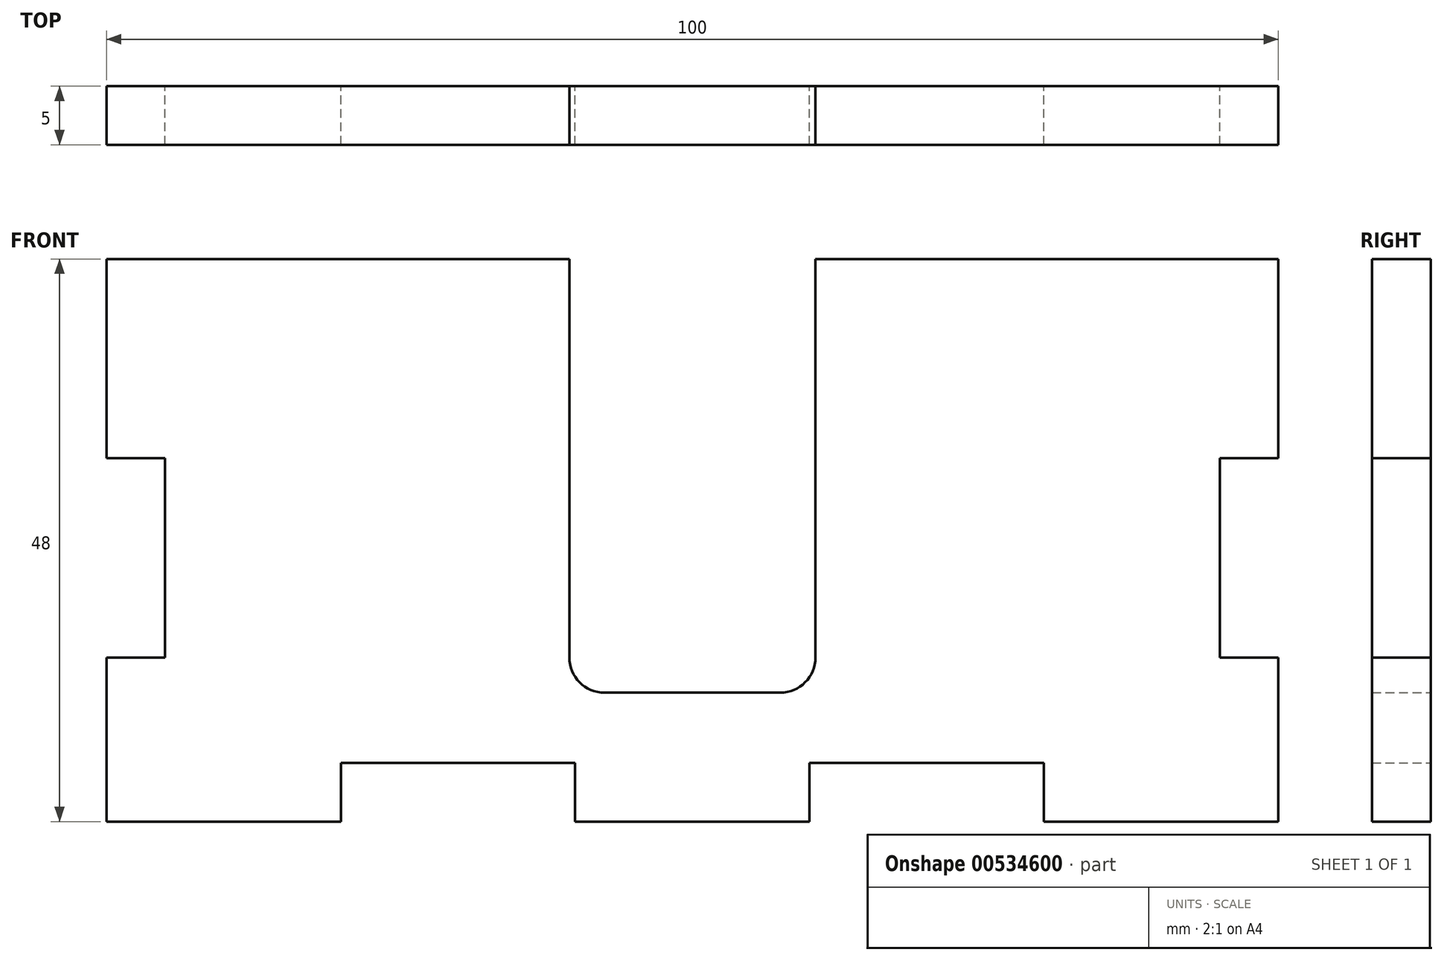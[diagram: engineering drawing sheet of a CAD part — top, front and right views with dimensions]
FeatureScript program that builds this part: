
annotation { "Feature Type Name" : "Feature", "Feature Type Description" : "" }
export const myFeature = defineFeature(function(context is Context, id is Id, definition is map)
    precondition{}
    {
        {
            var Q0;
            Q0=qCreatedBy(makeId("Front.planeOp"),FACE);
            var sketch = newSketch(context, id + "F0", { "sketchPlane" : qUnion([Q0])});
            skLineSegment(sketch, "E0.bottom", {"start": v(45, 21.5) * mm, "end": v(10.5, 21.5) * mm});
            skLineSegment(sketch, "E0.top", {"start": v(30, -21.5) * mm, "end": v(10, -21.5) * mm});
            skLineSegment(sketch, "E0.left", {"start": v(45, 4.5) * mm, "end": v(45, -12.5) * mm});
            skLineSegment(sketch, "E0.right", {"start": v(-45, 4.5) * mm, "end": v(-45, -12.5) * mm});
            skPoint(sketch, "E0.middle", {"position": v(0, 0) * mm});
            skLineSegment(sketch, "E1", {"start": v(-10.5, 21.5) * mm, "end": v(-10.5, -12.5) * mm});
            skLineSegment(sketch, "E2", {"start": v(-7.5, -15.5) * mm, "end": v(7.5, -15.5) * mm});
            skLineSegment(sketch, "E3", {"start": v(10.5, -12.5) * mm, "end": v(10.5, 21.5) * mm});
            skLineSegment(sketch, "E4.trimOffspring", {"start": v(-10.5, 21.5) * mm, "end": v(-45, 21.5) * mm});
            skPoint(sketch, "E5.visualSharp", {"position": v(-10.5, -15.5) * mm});
            skArc(sketch, "E5.filletArc", {"start": v(-10.5, -12.5) * mm, "mid": v(-9.62, -14.62) * mm, "end": v(-7.5, -15.5) * mm});
            skPoint(sketch, "E6.visualSharp", {"position": v(10.5, -15.5) * mm});
            skArc(sketch, "E6.filletArc", {"start": v(7.5, -15.5) * mm, "mid": v(9.62, -14.62) * mm, "end": v(10.5, -12.5) * mm});
            skLineSegment(sketch, "E7", {"start": v(-45, 21.5) * mm, "end": v(-50, 21.5) * mm, "construction": true});
            skLineSegment(sketch, "E8", {"start": v(-50, 21.5) * mm, "end": v(-50, -26.5) * mm, "construction": true});
            skLineSegment(sketch, "E9", {"start": v(-50, -26.5) * mm, "end": v(50, -26.5) * mm, "construction": true});
            skLineSegment(sketch, "E10", {"start": v(50, -26.5) * mm, "end": v(50, 21.5) * mm, "construction": true});
            skLineSegment(sketch, "E11", {"start": v(50, 21.5) * mm, "end": v(45, 21.5) * mm, "construction": true});
            skLineSegment(sketch, "E12.bottom", {"start": v(-45, 21.5) * mm, "end": v(-50, 21.5) * mm});
            skLineSegment(sketch, "E12.top", {"start": v(-45, 4.5) * mm, "end": v(-50, 4.5) * mm});
            skLineSegment(sketch, "E12.right", {"start": v(-50, 21.5) * mm, "end": v(-50, 4.5) * mm});
            skLineSegment(sketch, "E13.bottom", {"start": v(-45, -12.5) * mm, "end": v(-50, -12.5) * mm});
            skLineSegment(sketch, "E13.top", {"start": v(-45, -26.5) * mm, "end": v(-50, -26.5) * mm});
            skLineSegment(sketch, "E13.right", {"start": v(-50, -12.5) * mm, "end": v(-50, -26.5) * mm});
            skLineSegment(sketch, "E14.bottom", {"start": v(-50, -26.5) * mm, "end": v(-30, -26.5) * mm});
            skLineSegment(sketch, "E14.left", {"start": v(-50, -26.5) * mm, "end": v(-50, -23) * mm});
            skLineSegment(sketch, "E14.right", {"start": v(-30, -26.5) * mm, "end": v(-30, -21.5) * mm});
            skLineSegment(sketch, "E15.top", {"start": v(-10, -26.5) * mm, "end": v(10, -26.5) * mm});
            skLineSegment(sketch, "E15.left", {"start": v(-10, -21.5) * mm, "end": v(-10, -26.5) * mm});
            skLineSegment(sketch, "E15.right", {"start": v(10, -21.5) * mm, "end": v(10, -26.5) * mm});
            skLineSegment(sketch, "E16.top", {"start": v(30, -26.5) * mm, "end": v(50, -26.5) * mm});
            skLineSegment(sketch, "E16.left", {"start": v(30, -21.5) * mm, "end": v(30, -26.5) * mm});
            skLineSegment(sketch, "E16.right", {"start": v(50, -23) * mm, "end": v(50, -26.5) * mm});
            skPoint(sketch, "E13.left.start.orphan", {"position": v(-45, -21.5) * mm});
            skLineSegment(sketch, "E17.trimOffspring", {"start": v(-10, -21.5) * mm, "end": v(-30, -21.5) * mm});
            skLineSegment(sketch, "E18.MirrorCS", {"start": v(45, 21.5) * mm, "end": v(50, 21.5) * mm, "construction": true});
            skLineSegment(sketch, "E19.MirrorCS", {"start": v(45, 4.5) * mm, "end": v(50, 4.5) * mm});
            skLineSegment(sketch, "E20.MirrorCS", {"start": v(45, -12.5) * mm, "end": v(50, -12.5) * mm});
            skLineSegment(sketch, "E21", {"start": v(50, 21.5) * mm, "end": v(50, 4.5) * mm});
            skLineSegment(sketch, "E22", {"start": v(50, -12.5) * mm, "end": v(50, -26.5) * mm});
            skLineSegment(sketch, "E23", {"start": v(45, 21.5) * mm, "end": v(50, 21.5) * mm});
            skPoint(sketch, "E24.orphan", {"position": v(45, -21.5) * mm});
            skSolve(sketch);
        }
        {
            var Q0;
            Q0 = qSketchRegion(id + "F0", true);
            extrude(context, id + "F1", {"entities" : qUnion([Q0]), "depth" : 5 * mm, "offsetDistance" : 25 * mm});
        }
    });
